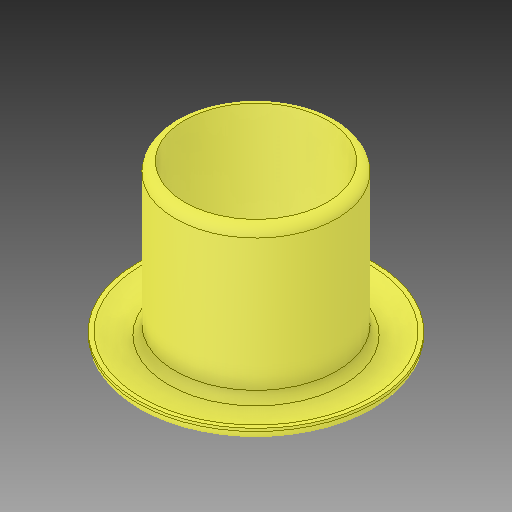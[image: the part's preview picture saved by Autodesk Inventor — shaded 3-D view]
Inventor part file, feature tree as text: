
AUTODESK INVENTOR PART (.ipt)
format: ipt  version: 2019.1 (Build 231200000, 200)  size: 208,896 bytes
history: mixed  units: in
note: dims shown in document units (in); Inventor stores cm internally (conversion verified against a paired STEP export)
features: fillet x1, imported_body x1
ambient origin geometry x8: Origin, YZ Plane, XZ Plane, XY Plane, X Axis, Y Axis, Z Axis, Center Point
bodies: Solid1 (imported_parasolid)
feature tree (2):
  fillet  "Fillet1"  [1 undecoded]
  imported_body  NMx_Import_Brep_tag  [imported B-rep: ~2 faces, bbox_mm=None]
note: 1 required parameter value undecoded (feature->parameter linkage not recoverable at this tier; creation-order binding heuristic only, values carry confidence <= 0.55)
